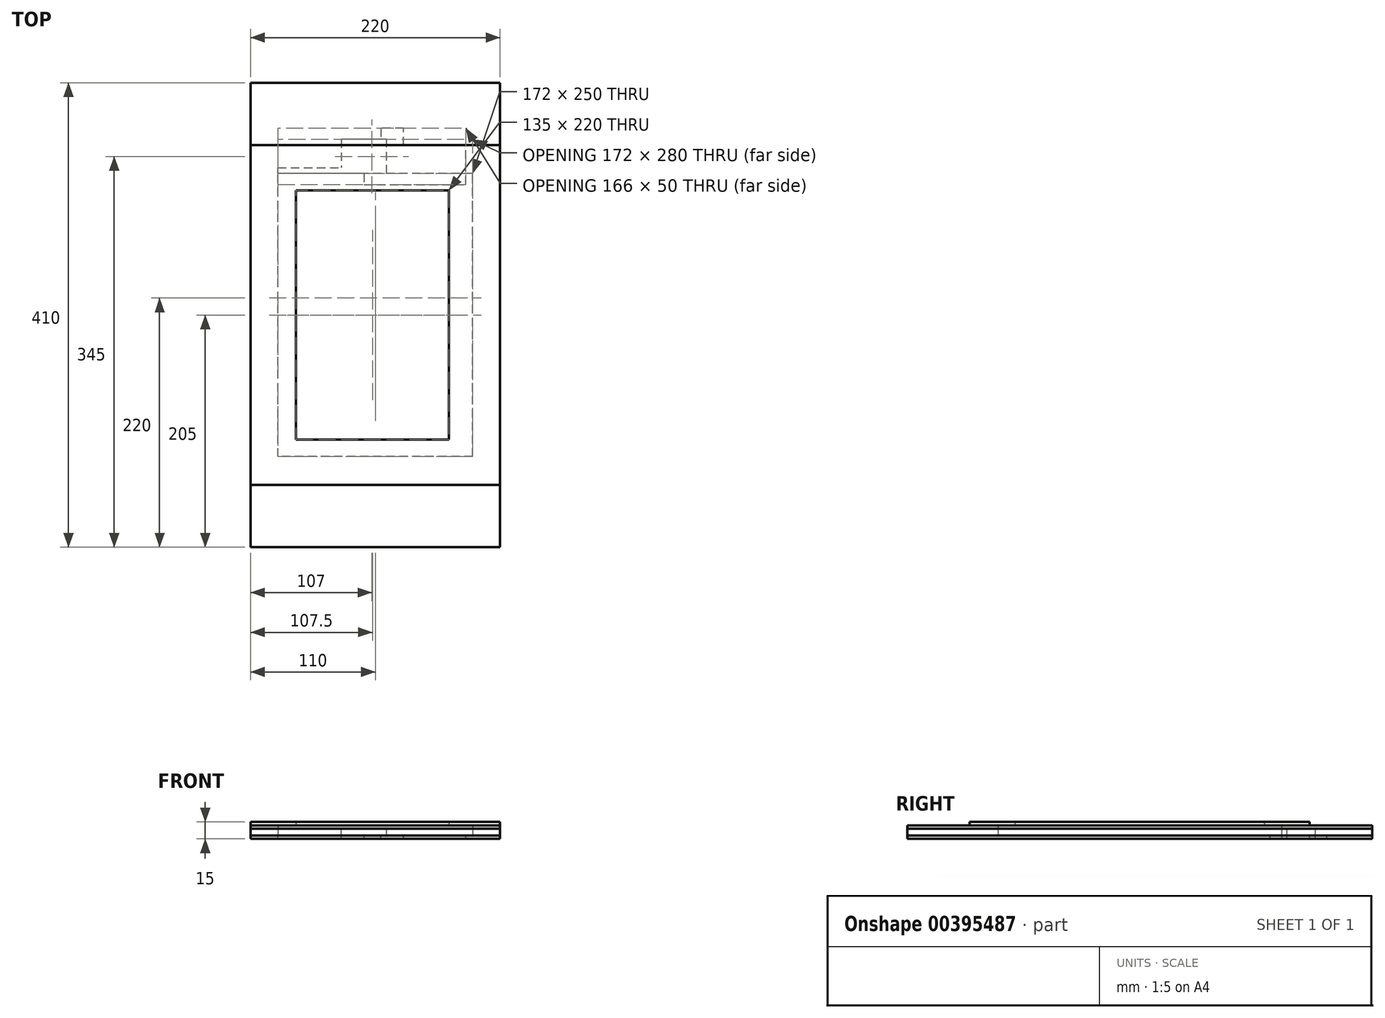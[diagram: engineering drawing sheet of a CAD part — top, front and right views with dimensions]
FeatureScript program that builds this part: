
annotation { "Feature Type Name" : "Feature", "Feature Type Description" : "" }
export const myFeature = defineFeature(function(context is Context, id is Id, definition is map)
    precondition{}
    {
        {
            var Q0;
            Q0=qCreatedBy(makeId("Top.planeOp"),FACE);
            var sketch = newSketch(context, id + "F0", { "sketchPlane" : qUnion([Q0])});
            skLineSegment(sketch, "E0.bottom", {"start": v(110, -205) * mm, "end": v(-110, -205) * mm});
            skLineSegment(sketch, "E0.top", {"start": v(110, 205) * mm, "end": v(-110, 205) * mm});
            skLineSegment(sketch, "E0.left", {"start": v(110, -205) * mm, "end": v(110, 205) * mm});
            skLineSegment(sketch, "E0.right", {"start": v(-110, -205) * mm, "end": v(-110, 205) * mm});
            skPoint(sketch, "E0.middle", {"position": v(0, 0) * mm});
            skSolve(sketch);
        }
        {
            var Q0;
            Q0 = qSketchRegion(id + "F0", true);
            extrude(context, id + "F1", {"entities" : qUnion([Q0]), "depth" : 3 * mm});
        }
        {
            var Q0;
            Q0=makeQuery(id+"F1.opExtrude","CAP_FACE",FACE,{"disambiguationData":[OSD([sQuery(id+"F0.wireOp",EDGE,"E0.bottom"),sQuery(id+"F0.wireOp",EDGE,"E0.top"),sQuery(id+"F0.wireOp",EDGE,"E0.left"),sQuery(id+"F0.wireOp",EDGE,"E0.right")])],"isStart":false});
            var sketch = newSketch(context, id + "F2", { "sketchPlane" : qUnion([Q0])});
            skLineSegment(sketch, "E1.bottom", {"start": v(-110, 205) * mm, "end": v(110, 205) * mm});
            skLineSegment(sketch, "E1.top", {"start": v(-110, -205) * mm, "end": v(110, -205) * mm});
            skLineSegment(sketch, "E1.left", {"start": v(-110, 205) * mm, "end": v(-110, -205) * mm});
            skLineSegment(sketch, "E1.right", {"start": v(110, 205) * mm, "end": v(110, -205) * mm});
            skLineSegment(sketch, "E2.bottom", {"start": v(86, -125) * mm, "end": v(-86, -125) * mm});
            skLineSegment(sketch, "E2.top", {"start": v(86, 125) * mm, "end": v(-86, 125) * mm});
            skLineSegment(sketch, "E2.left", {"start": v(86, -125) * mm, "end": v(86, 125) * mm});
            skLineSegment(sketch, "E2.right", {"start": v(-86, -125) * mm, "end": v(-86, 125) * mm});
            skPoint(sketch, "E2.middle", {"position": v(0, 0) * mm});
            skSolve(sketch);
        }
        {
            var Q0;
            Q0 = qSketchRegion(id + "F2", true);
            extrude(context, id + "F3", {"entities" : qUnion([Q0]), "depth" : 6 * mm});
        }
        {
            var Q0;
            Q0=makeQuery(id+"F3.opExtrude","CAP_FACE",FACE,{"disambiguationData":[OSD([sQuery(id+"F2.wireOp",EDGE,"E1.bottom"),sQuery(id+"F2.wireOp",EDGE,"E1.top"),sQuery(id+"F2.wireOp",EDGE,"E1.left"),sQuery(id+"F2.wireOp",EDGE,"E1.right"),sQuery(id+"F2.wireOp",EDGE,"E2.bottom"),sQuery(id+"F2.wireOp",EDGE,"E2.top"),sQuery(id+"F2.wireOp",EDGE,"E2.left"),sQuery(id+"F2.wireOp",EDGE,"E2.right")])],"isStart":false});
            var sketch = newSketch(context, id + "F4", { "sketchPlane" : qUnion([Q0])});
            skLineSegment(sketch, "E3.bottom", {"start": v(-110, 150) * mm, "end": v(110, 150) * mm});
            skLineSegment(sketch, "E3.top", {"start": v(-110, -150) * mm, "end": v(110, -150) * mm});
            skLineSegment(sketch, "E3.left", {"start": v(-110, 150) * mm, "end": v(-110, -150) * mm});
            skLineSegment(sketch, "E3.right", {"start": v(110, 150) * mm, "end": v(110, -150) * mm});
            skLineSegment(sketch, "E4.bottom", {"start": v(65, -110) * mm, "end": v(-70, -110) * mm});
            skLineSegment(sketch, "E4.top", {"start": v(65, 110) * mm, "end": v(-70, 110) * mm});
            skLineSegment(sketch, "E4.left", {"start": v(65, -110) * mm, "end": v(65, 110) * mm});
            skLineSegment(sketch, "E4.right", {"start": v(-70, -110) * mm, "end": v(-70, 110) * mm});
            skPoint(sketch, "E4.middle", {"position": v(0, 0) * mm});
            skLineSegment(sketch, "E5", {"start": v(-70, 110) * mm, "end": v(-70, 150) * mm, "construction": true});
            skLineSegment(sketch, "E6", {"start": v(-70, -110) * mm, "end": v(-70, -150) * mm, "construction": true});
            skLineSegment(sketch, "E7", {"start": v(-110, 150) * mm, "end": v(110, -150) * mm, "construction": true});
            skSolve(sketch);
        }
        {
            var Q0;
            Q0 = qSketchRegion(id + "F4", true);
            extrude(context, id + "F5", {"entities" : qUnion([Q0]), "depth" : 3 * mm});
        }
        {
            var Q0;
            Q0=makeQuery(id+"F1.opExtrude","CAP_FACE",FACE,{"disambiguationData":[OSD([sQuery(id+"F0.wireOp",EDGE,"E0.bottom"),sQuery(id+"F0.wireOp",EDGE,"E0.top"),sQuery(id+"F0.wireOp",EDGE,"E0.left"),sQuery(id+"F0.wireOp",EDGE,"E0.right")])],"isStart":false});
            var sketch = newSketch(context, id + "F6", { "sketchPlane" : qUnion([Q0])});
            skLineSegment(sketch, "E8", {"start": v(-10, 150) * mm, "end": v(-10, 115) * mm});
            skLineSegment(sketch, "E9", {"start": v(-10, 115) * mm, "end": v(80, 115) * mm});
            skLineSegment(sketch, "E10", {"start": v(80, 115) * mm, "end": v(80, 150) * mm});
            skLineSegment(sketch, "E11", {"start": v(80, 150) * mm, "end": v(25, 150) * mm});
            skLineSegment(sketch, "E12", {"start": v(25, 150) * mm, "end": v(25, 165) * mm});
            skLineSegment(sketch, "E13", {"start": v(25, 165) * mm, "end": v(5, 165) * mm});
            skLineSegment(sketch, "E14", {"start": v(5, 165) * mm, "end": v(5, 150) * mm});
            skLineSegment(sketch, "E15", {"start": v(5, 150) * mm, "end": v(-10, 150) * mm});
            skSolve(sketch);
        }
        {
            var Q0;
            Q0=makeQuery(id+"F6.imprint","IMPRINT",FACE,{"disambiguationData":[TD([[makeQuery(id+"F6.imprint","IMPRINT",EDGE,{"derivedFrom":sQuery(id+"F6.wireOp",EDGE,"E8")}),1.0]])]});
            extrude(context, id + "F7", {"entities" : qUnion([Q0]), "operationType" : NewBodyOperationType.REMOVE, "oppositeDirection" : true, "depth" : 25 * mm});
        }
        {
            var Q0;
            Q0=makeQuery(id+"F3.opExtrude","CAP_FACE",FACE,{"disambiguationData":[OSD([sQuery(id+"F2.wireOp",EDGE,"E1.bottom"),sQuery(id+"F2.wireOp",EDGE,"E1.top"),sQuery(id+"F2.wireOp",EDGE,"E1.left"),sQuery(id+"F2.wireOp",EDGE,"E1.right"),sQuery(id+"F2.wireOp",EDGE,"E2.bottom"),sQuery(id+"F2.wireOp",EDGE,"E2.top"),sQuery(id+"F2.wireOp",EDGE,"E2.left"),sQuery(id+"F2.wireOp",EDGE,"E2.right")])],"isStart":false});
            var sketch = newSketch(context, id + "F8", { "sketchPlane" : qUnion([Q0])});
            skLineSegment(sketch, "E16.bottom", {"start": v(-110, 205) * mm, "end": v(110, 205) * mm});
            skLineSegment(sketch, "E16.top", {"start": v(-110, -205) * mm, "end": v(110, -205) * mm});
            skLineSegment(sketch, "E16.left", {"start": v(-110, 205) * mm, "end": v(-110, -205) * mm});
            skLineSegment(sketch, "E16.right", {"start": v(110, 205) * mm, "end": v(110, -205) * mm});
            skLineSegment(sketch, "E17.bottom", {"start": v(86, -125) * mm, "end": v(-86, -125) * mm});
            skLineSegment(sketch, "E17.top", {"start": v(86, 125) * mm, "end": v(-86, 125) * mm});
            skLineSegment(sketch, "E17.left", {"start": v(86, -125) * mm, "end": v(86, 125) * mm});
            skLineSegment(sketch, "E17.right", {"start": v(-86, -125) * mm, "end": v(-86, 125) * mm});
            skPoint(sketch, "E17.middle", {"position": v(0, 0) * mm});
            skSolve(sketch);
        }
        {
            var Q0;
            Q0 = qSketchRegion(id + "F8", true);
            extrude(context, id + "F9", {"entities" : qUnion([Q0]), "depth" : 3 * mm});
        }
        {
            var Q0;
            Q0=makeQuery(id+"F5.opExtrude","SWEPT_BODY",BODY,{"disambiguationData":[OSD([sQuery(id+"F4.wireOp",EDGE,"E3.bottom"),sQuery(id+"F4.wireOp",EDGE,"E3.top"),sQuery(id+"F4.wireOp",EDGE,"E3.left"),sQuery(id+"F4.wireOp",EDGE,"E3.right"),sQuery(id+"F4.wireOp",EDGE,"E4.bottom"),sQuery(id+"F4.wireOp",EDGE,"E4.top"),sQuery(id+"F4.wireOp",EDGE,"E4.left"),sQuery(id+"F4.wireOp",EDGE,"E4.right")])]});
            transform(context, id + "F10", {"entities" : qUnion([Q0]), "transformType" : TransformType.TRANSLATION_3D, "dx" : 0 * mm, "dy" : 0 * mm, "dz" : 3 * mm, "makeCopy" : false});
        }
        {
            var Q0;
            Q0=makeQuery(id+"F3.opExtrude","CAP_FACE",FACE,{"disambiguationData":[OSD([sQuery(id+"F2.wireOp",EDGE,"E1.bottom"),sQuery(id+"F2.wireOp",EDGE,"E1.top"),sQuery(id+"F2.wireOp",EDGE,"E1.left"),sQuery(id+"F2.wireOp",EDGE,"E1.right"),sQuery(id+"F2.wireOp",EDGE,"E2.bottom"),sQuery(id+"F2.wireOp",EDGE,"E2.top"),sQuery(id+"F2.wireOp",EDGE,"E2.left"),sQuery(id+"F2.wireOp",EDGE,"E2.right")])],"isStart":false});
            var sketch = newSketch(context, id + "F11", { "sketchPlane" : qUnion([Q0])});
            skLineSegment(sketch, "E18", {"start": v(-30, 155) * mm, "end": v(-30, 125) * mm});
            skLineSegment(sketch, "E19", {"start": v(-30, 125) * mm, "end": v(10, 125) * mm});
            skLineSegment(sketch, "E20", {"start": v(10, 125) * mm, "end": v(10, 155) * mm});
            skLineSegment(sketch, "E21", {"start": v(10, 155) * mm, "end": v(-30, 155) * mm});
            skSolve(sketch);
        }
        {
            var Q0;
            Q0=makeQuery(id+"F11.imprint","IMPRINT",FACE,{"disambiguationData":[TD([[makeQuery(id+"F11.imprint","IMPRINT",EDGE,{"derivedFrom":sQuery(id+"F11.wireOp",EDGE,"E18")}),1.0]])]});
            extrude(context, id + "F12", {"entities" : qUnion([Q0]), "operationType" : NewBodyOperationType.REMOVE, "oppositeDirection" : true, "depth" : 25 * mm});
        }
        {
            var Q0;
            Q0=makeQuery(id+"F3.opExtrude","CAP_FACE",FACE,{"disambiguationData":[OSD([sQuery(id+"F2.wireOp",EDGE,"E1.bottom"),sQuery(id+"F2.wireOp",EDGE,"E1.top"),sQuery(id+"F2.wireOp",EDGE,"E1.left"),sQuery(id+"F2.wireOp",EDGE,"E1.right"),sQuery(id+"F2.wireOp",EDGE,"E2.bottom"),sQuery(id+"F2.wireOp",EDGE,"E2.top"),sQuery(id+"F2.wireOp",EDGE,"E2.left"),sQuery(id+"F2.wireOp",EDGE,"E2.right")])],"isStart":false});
            var sketch = newSketch(context, id + "F13", { "sketchPlane" : qUnion([Q0])});
            skLineSegment(sketch, "E22.bottom", {"start": v(-86, 125) * mm, "end": v(-30, 125) * mm});
            skLineSegment(sketch, "E22.top", {"start": v(-86, 130) * mm, "end": v(-30, 130) * mm});
            skLineSegment(sketch, "E22.left", {"start": v(-86, 125) * mm, "end": v(-86, 130) * mm});
            skLineSegment(sketch, "E22.right", {"start": v(-30, 125) * mm, "end": v(-30, 130) * mm});
            skSolve(sketch);
        }
        {
            var Q0;
            Q0=makeQuery(id+"F13.imprint","IMPRINT",FACE,{"disambiguationData":[TD([[makeQuery(id+"F13.imprint","IMPRINT",EDGE,{"derivedFrom":sQuery(id+"F13.wireOp",EDGE,"E22.bottom")}),-1.0]])]});
            extrude(context, id + "F14", {"entities" : qUnion([Q0]), "operationType" : NewBodyOperationType.REMOVE, "oppositeDirection" : true, "depth" : 25 * mm});
        }
    });
